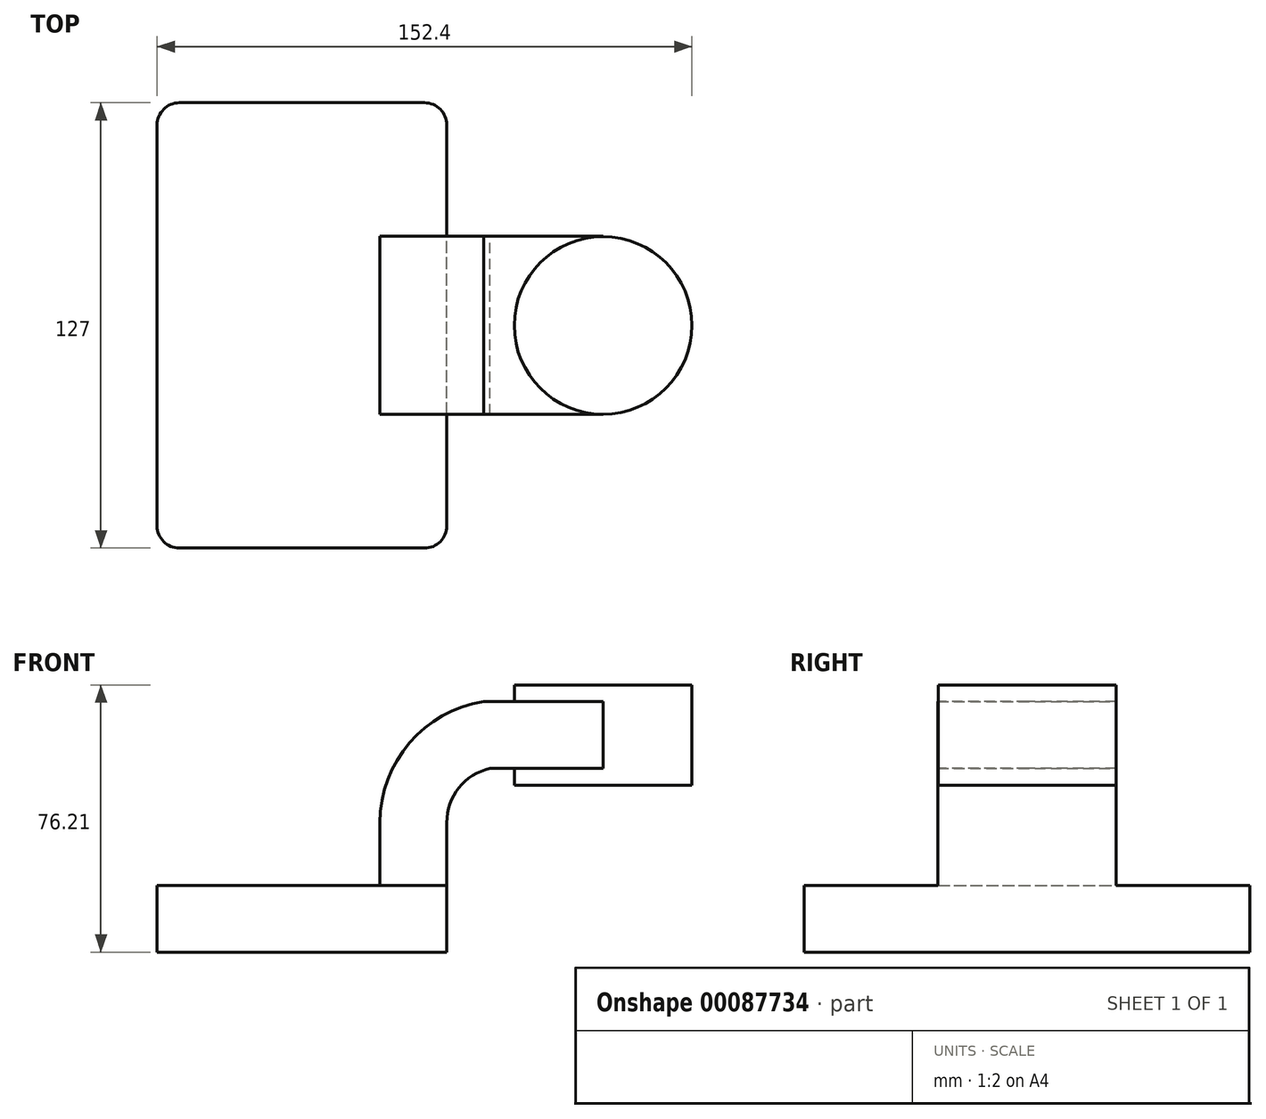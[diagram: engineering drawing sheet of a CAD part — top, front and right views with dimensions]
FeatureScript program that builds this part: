
annotation { "Feature Type Name" : "Feature", "Feature Type Description" : "" }
export const myFeature = defineFeature(function(context is Context, id is Id, definition is map)
    precondition{}
    {
        {
            var Q0;
            Q0=qCreatedBy(makeId("Front.planeOp"),FACE);
            var sketch = newSketch(context, id + "F0", { "sketchPlane" : qUnion([Q0])});
            skLineSegment(sketch, "E0.bottom", {"start": v(-41.28, -9.53) * mm, "end": v(41.28, -9.53) * mm});
            skLineSegment(sketch, "E0.top", {"start": v(-41.28, 9.53) * mm, "end": v(41.28, 9.53) * mm});
            skLineSegment(sketch, "E0.left", {"start": v(-41.28, -9.53) * mm, "end": v(-41.28, 9.53) * mm});
            skLineSegment(sketch, "E0.right", {"start": v(41.28, -9.53) * mm, "end": v(41.28, 9.53) * mm});
            skPoint(sketch, "E0.middle", {"position": v(0, 0) * mm});
            skLineSegment(sketch, "E1", {"start": v(41.28, 9.53) * mm, "end": v(41.28, 27.41) * mm});
            skArc(sketch, "E2", {"start": v(41.27, 27.41) * mm, "mid": v(44.72, 37.29) * mm, "end": v(53.56, 42.88) * mm});
            skLineSegment(sketch, "E3", {"start": v(53.56, 42.88) * mm, "end": v(86, 42.88) * mm});
            skLineSegment(sketch, "E4.bottom", {"start": v(60.32, 38.1) * mm, "end": v(111.12, 38.1) * mm});
            skLineSegment(sketch, "E4.top", {"start": v(60.32, 66.67) * mm, "end": v(111.12, 66.67) * mm});
            skLineSegment(sketch, "E4.left", {"start": v(60.32, 38.1) * mm, "end": v(60.32, 66.67) * mm});
            skLineSegment(sketch, "E4.right", {"start": v(111.12, 38.1) * mm, "end": v(111.12, 66.67) * mm});
            skPoint(sketch, "E4.middle", {"position": v(85.72, 52.39) * mm});
            skLineSegment(sketch, "E5.0", {"start": v(51.8, 61.93) * mm, "end": v(85.8, 61.93) * mm});
            skArc(sketch, "E5.1", {"start": v(22.22, 27.41) * mm, "mid": v(30.63, 50.14) * mm, "end": v(51.8, 61.93) * mm});
            skLineSegment(sketch, "E5.2", {"start": v(22.22, 9.53) * mm, "end": v(22.22, 27.41) * mm});
            skLineSegment(sketch, "E6", {"start": v(85.8, 38.1) * mm, "end": v(85.8, 66.67) * mm});
            skFitSpline(sketch, "E7", {"points": [v(-41.28, 9.52) * mm, v(51.8, 61.93) * mm], "startDerivative": vector(0.82, 95.96) * mm, "endDerivative": vector(155.08, 0.1) * mm});
            skSolve(sketch);
        }
        {
            var Q0;
            Q0=makeQuery(id+"F0.imprint","IMPRINT",FACE,{"disambiguationData":[TD([[makeQuery(id+"F0.imprint","IMPRINT",EDGE,{"derivedFrom":sQuery(id+"F0.wireOp",EDGE,"E0.bottom")}),1.0]])]});
            extrude(context, id + "F1", {"entities" : qUnion([Q0]), "endBound" : BoundingType.SYMMETRIC, "depth" : 127 * mm});
        }
        {
            var Q0;
            {var subQ7=sQuery(id+"F0.wireOp",EDGE,"E1");Q0=makeQuery(id+"F0.imprint","IMPRINT",FACE,{"disambiguationData":[TD([[makeQuery(id+"F0.imprint","IMPRINT",EDGE,{"derivedFrom":subQ7}),1.0]])]});}
            var Q1;
            {var subQ0=sQuery(id+"F0.wireOp",EDGE,"E4.left");var subQ1=sQuery(id+"F0.wireOp",EDGE,"E3");var subQ2=makeQuery(id+"F0.imprint","INTERSECT",VERTEX,{"derivedFrom":[subQ1,subQ0]});Q1=makeQuery(id+"F0.imprint","IMPRINT",FACE,{"disambiguationData":[TD([[makeQuery(id+"F0.imprint","IMPRINT",EDGE,{"disambiguationData":[TD([[subQ2,-1.0]])],"derivedFrom":subQ1}),1.0]])]});}
            extrude(context, id + "F2", {"entities" : qUnion([Q0, Q1]), "operationType" : NewBodyOperationType.ADD, "endBound" : BoundingType.SYMMETRIC, "depth" : 50.8 * mm});
        }
        {
            var Q0;
            Q0=makeQuery(id+"F0.imprint","IMPRINT",FACE,{"disambiguationData":[TD([[makeQuery(id+"F0.imprint","IMPRINT",EDGE,{"derivedFrom":sQuery(id+"F0.wireOp",EDGE,"E5.1")}),1.0]])]});
            extrude(context, id + "F3", {"entities" : qUnion([Q0]), "operationType" : NewBodyOperationType.ADD, "endBound" : BoundingType.SYMMETRIC, "depth" : 15.88 * mm});
        }
        {
            var Q0;
            {var subQ4=sQuery(id+"F0.wireOp",EDGE,"E4.right");Q0=makeQuery(id+"F0.imprint","IMPRINT",FACE,{"disambiguationData":[TD([[makeQuery(id+"F0.imprint","IMPRINT",EDGE,{"derivedFrom":subQ4}),1.0]])]});}
            var Q1;
            Q1=sQuery(id+"F0.wireOp",EDGE,"E6");
            revolve(context, id + "F4", {"operationType" : NewBodyOperationType.ADD, "entities" : qUnion([Q0]), "axis" : qUnion([Q1]), "revolveType" : RevolveType.FULL});
        }
        {
            var Q0;
            Q0=makeQuery(id+"F1.opExtrude","CAP_EDGE",EDGE,{"disambiguationData":[OSD([sQuery(id+"F0.wireOp",EDGE,"E0.left")])],"isStart":false});
            var Q1;
            Q1=makeQuery(id+"F1.opExtrude","CAP_EDGE",EDGE,{"disambiguationData":[OSD([sQuery(id+"F0.wireOp",EDGE,"E0.right")])],"isStart":false});
            var Q2;
            Q2=makeQuery(id+"F1.opExtrude","CAP_EDGE",EDGE,{"disambiguationData":[OSD([sQuery(id+"F0.wireOp",EDGE,"E0.left")])],"isStart":true});
            var Q3;
            Q3=makeQuery(id+"F1.opExtrude","CAP_EDGE",EDGE,{"disambiguationData":[OSD([sQuery(id+"F0.wireOp",EDGE,"E0.right")])],"isStart":true});
            fillet(context, id + "F5", {"entities" : qUnion([Q0, Q1, Q2, Q3]), "radius" : 6.35 * mm, "tangentPropagation" : true, "allowEdgeOverflow" : false});
        }
    });
